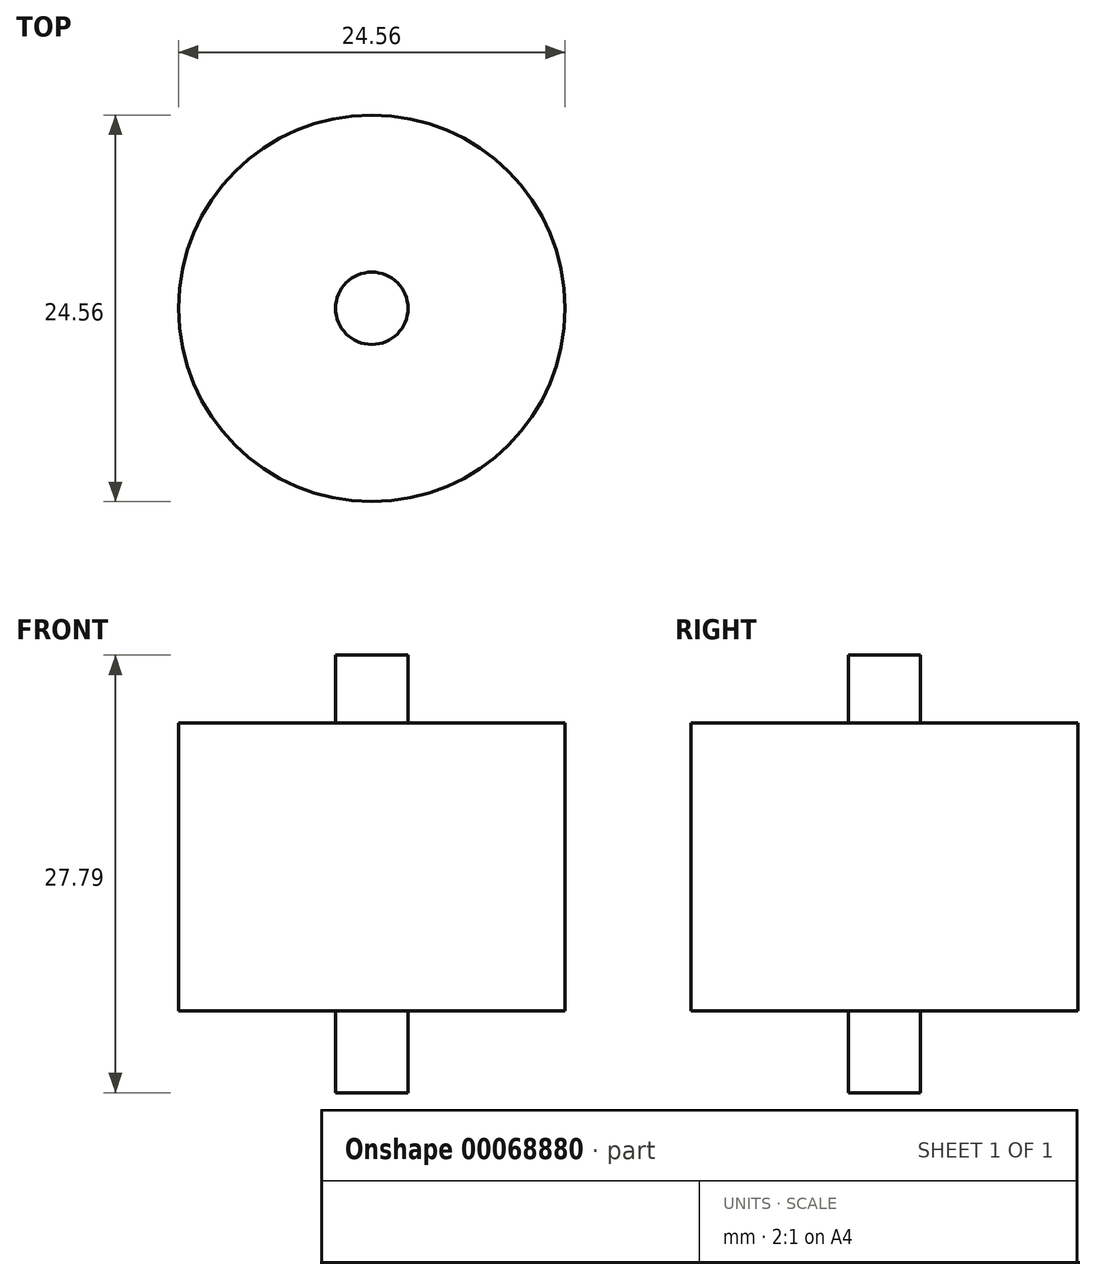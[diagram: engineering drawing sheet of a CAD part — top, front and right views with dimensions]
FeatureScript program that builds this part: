
annotation { "Feature Type Name" : "Feature", "Feature Type Description" : "" }
export const myFeature = defineFeature(function(context is Context, id is Id, definition is map)
    precondition{}
    {
        {
            var Q0;
            Q0=qCreatedBy(makeId("Top.planeOp"),FACE);
            var sketch = newSketch(context, id + "F0", { "sketchPlane" : qUnion([Q0])});
            skCircle(sketch, "E0", {"center": v(0, 0) * mm, "radius": 12.28 * mm});
            skSolve(sketch);
        }
        {
            var Q0;
            Q0 = qSketchRegion(id + "F0", true);
            extrude(context, id + "F1", {"entities" : qUnion([Q0]), "depth" : 18.26 * mm});
        }
        {
            var Q0;
            Q0=makeQuery(id+"F1.opExtrude","CAP_FACE",FACE,{"disambiguationData":[OSD([sQuery(id+"F0.wireOp",EDGE,"E0")])],"isStart":false});
            var sketch = newSketch(context, id + "F2", { "sketchPlane" : qUnion([Q0])});
            skCircle(sketch, "E1", {"center": v(0, 0) * mm, "radius": 2.3 * mm});
            skSolve(sketch);
        }
        {
            var Q0;
            Q0 = qSketchRegion(id + "F2", true);
            extrude(context, id + "F3", {"entities" : qUnion([Q0]), "operationType" : NewBodyOperationType.ADD, "depth" : 4.32 * mm});
        }
        {
            var Q0;
            Q0=makeQuery(id+"F3.opExtrude","CAP_FACE",FACE,{"disambiguationData":[OSD([sQuery(id+"F2.wireOp",EDGE,"E1")])],"isStart":false});
            extrude(context, id + "F4", {"entities" : qUnion([Q0]), "operationType" : NewBodyOperationType.ADD, "oppositeDirection" : true, "depth" : 27.79 * mm});
        }
    });
